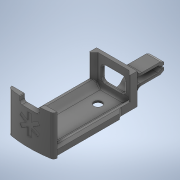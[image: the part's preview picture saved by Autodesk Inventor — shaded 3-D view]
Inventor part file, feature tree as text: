
AUTODESK INVENTOR PART (.ipt)
format: ipt  version: 2020 (Build 240168000, 168)  size: 799,744 bytes
history: native  units: mm
features: projected_geometry x32, extrude x18, sketch x16, fillet x10, other x9, chamfer x2
ambient origin geometry x8: Origin, YZ Plane, XZ Plane, XY Plane, X Axis, Y Axis, Z Axis, Center Point
bodies: Body1 (feature_tree)
feature tree (87):
  other  "Твердое тело1"
  sketch  "Эскиз1"
  extrude  "Выдавливание3"  Depth=202.0mm
  other  "РабПлоскость1"
  extrude  "Выдавливание1"  Depth=35.0mm
  other  "РабПлоскость2"
  sketch  "Эскиз2"
  extrude  "Выдавливание4"  Depth=68.0mm
  extrude  "Выдавливание5"  Depth=2.0mm
  sketch  "Эскиз4"
  extrude  "Выдавливание6"  Depth=2.0mm
  extrude  "Выдавливание7"  Depth=3.0mm
  other  "РабПлоскость3"
  extrude  "Выдавливание8"  Depth=3.0mm
  other  "РабПлоскость4"
  extrude  "Выдавливание9"  Depth=210.0mm
  sketch  "Эскиз8"
  extrude  "Выдавливание10"  Depth=20.0mm TaperAngle=0.0deg
  fillet  "Сопряжение1"  Radius=1.5mm
  fillet  "Сопряжение2"  Radius=28.0mm
  fillet  "Сопряжение3"  Radius=7.0mm
  fillet  "Сопряжение4"  Radius=20.0mm
  fillet  "Сопряжение5"  Radius=13.0mm
  extrude  "Выдавливание11"  Depth=5.0mm
  extrude  "Выдавливание12"  Depth=3.0mm
  fillet  "Сопряжение6"  Radius=10.0mm
  extrude  "Выдавливание13"  Depth=84.0mm
  chamfer  "Фаска1"  Distance=5.0mm
  fillet  "Сопряжение7"  Radius=52.0mm
  sketch  "Эскиз10"
  other  "РабПлоскость5"
  extrude  "Выдавливание14"  Depth=5.0mm TaperAngle=0.0deg
  fillet  "Сопряжение8"  Radius=35.0mm
  extrude  "Выдавливание15"  Depth=18.0mm
  fillet  "Сопряжение9"  Radius=3.0mm
  extrude  "Выдавливание16"  Depth=30.0mm TaperAngle=360.0deg
  fillet  "Сопряжение10"  Radius=0.5mm
  extrude  "Выдавливание17"  TaperAngle=0.0deg  [1 undecoded]
  chamfer  "Фаска2"  Distance=8.0mm
  other  "РабПлоскость10"
  other  "РабПлоскость9"
  sketch  "Эскиз14"
  other  "РабПлоскость8"
  sketch  "Эскиз15"
  sketch  "Эскиз16"
  sketch  "Эскиз17"
  extrude  "Выдавливание20"  Depth=2.0mm
  extrude  "Выдавливание21"  Depth=1.5mm TaperAngle=0.0deg
  projected_geometry  "Спроецированная петля1"
  projected_geometry  "Спроецированная петля7"
  projected_geometry  "Спроецированная петля8"
  sketch  "Эскиз3"
  projected_geometry  "Спроецированная петля9"
  projected_geometry  "Спроецированная петля10"
  projected_geometry  "Спроецированная петля11"
  projected_geometry  "Спроецированная петля12"
  sketch  "Эскиз5"
  projected_geometry  "Спроецированная петля13"
  projected_geometry  "Спроецированная петля14"
  projected_geometry  "Спроецированная петля15"
  projected_geometry  "Спроецированная петля16"
  projected_geometry  "Спроецированная петля17"
  sketch  "Эскиз6"
  projected_geometry  "Спроецированная петля18"
  projected_geometry  "Спроецированная петля19"
  projected_geometry  "Спроецированная петля20"
  projected_geometry  "Спроецированная петля21"
  projected_geometry  "Спроецированная петля22"
  projected_geometry  "Спроецированная петля23"
  projected_geometry  "Спроецированная петля24"
  projected_geometry  "Спроецированная петля25"
  projected_geometry  "Спроецированная петля26"
  projected_geometry  "Спроецированная петля27"
  projected_geometry  "Спроецированная петля28"
  sketch  "Эскиз9"
  projected_geometry  "Спроецированная петля29"
  projected_geometry  "Спроецированная петля30"
  sketch  "Эскиз11"
  projected_geometry  "Спроецированная петля31"
  projected_geometry  "Спроецированная петля32"
  projected_geometry  "Спроецированная петля33"
  sketch  "Эскиз12"
  projected_geometry  "Спроецированная петля34"
  projected_geometry  "Спроецированная петля35"
  projected_geometry  "Спроецированная петля37"
  sketch  "Эскиз18"
  projected_geometry  "Спроецированная петля38"
note: 1 required parameter value undecoded (feature->parameter linkage not recoverable at this tier; creation-order binding heuristic only, values carry confidence <= 0.55)
